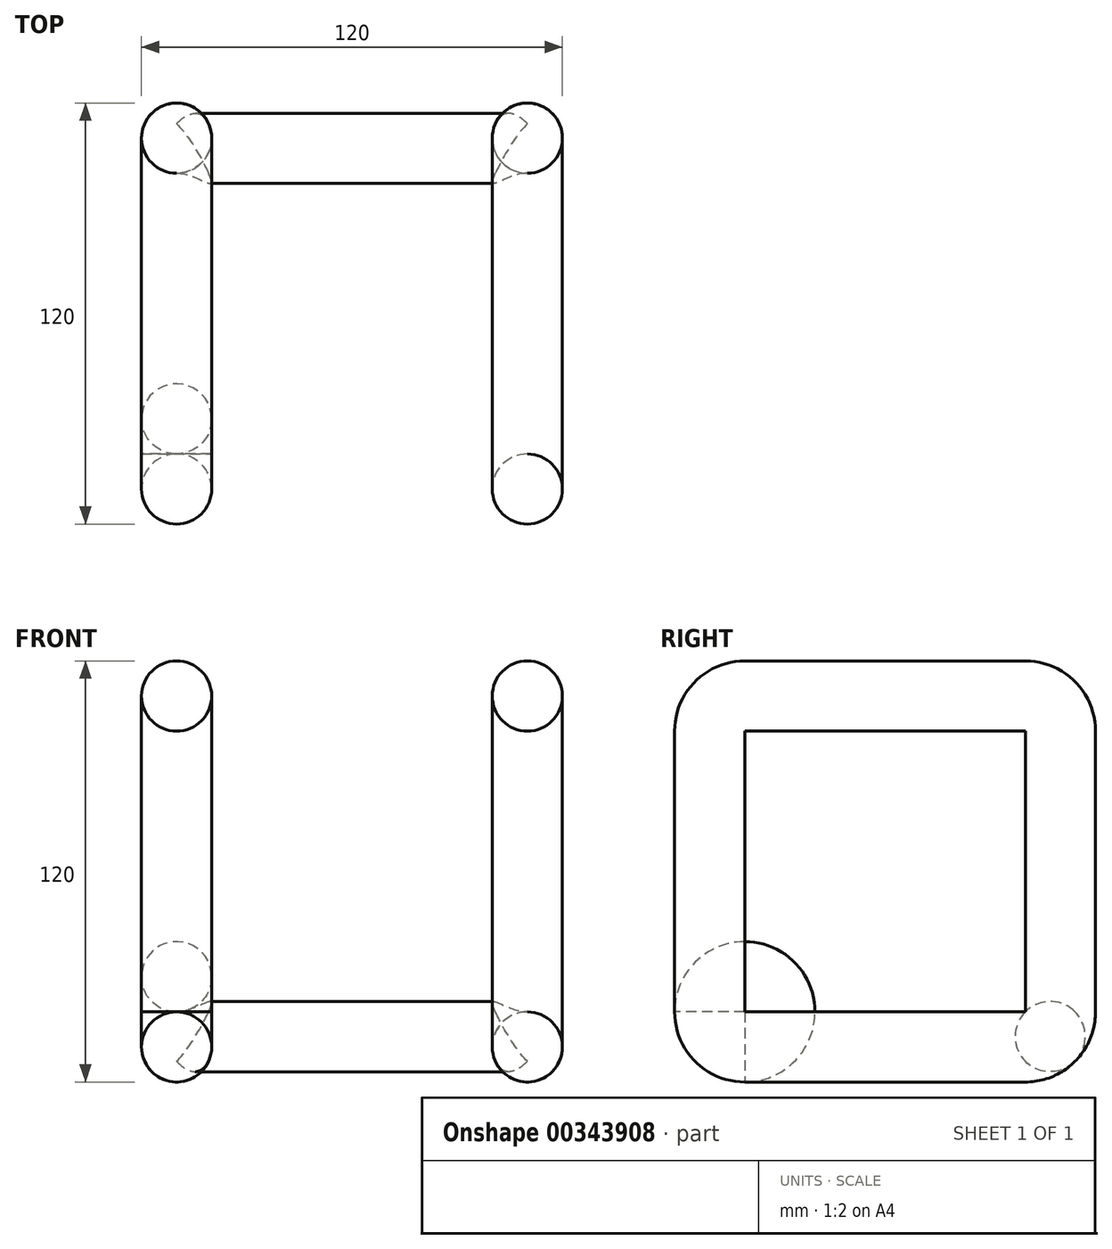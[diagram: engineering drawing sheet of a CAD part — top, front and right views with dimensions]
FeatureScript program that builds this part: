
annotation { "Feature Type Name" : "Feature", "Feature Type Description" : "" }
export const myFeature = defineFeature(function(context is Context, id is Id, definition is map)
    precondition{}
    {
        {
            var Q0;
            Q0=qCreatedBy(makeId("Front.planeOp"),FACE);
            var sketch = newSketch(context, id + "F0", { "sketchPlane" : qUnion([Q0])});
            skCircle(sketch, "E0", {"center": v(0, 0) * mm, "radius": 10 * mm});
            skSolve(sketch);
        }
        {
            var Q0;
            Q0 = qSketchRegion(id + "F0", true);
            extrude(context, id + "F1", {"entities" : qUnion([Q0]), "endBound" : BoundingType.SYMMETRIC, "depth" : 80 * mm});
        }
        {
            var Q0;
            Q0=makeQuery(id+"F1.opExtrude","CAP_FACE",FACE,{"disambiguationData":[OSD([sQuery(id+"F0.wireOp",EDGE,"E0")])],"isStart":true});
            var sketch = newSketch(context, id + "F2", { "sketchPlane" : qUnion([Q0])});
            skCircle(sketch, "E1", {"center": v(0, 0) * mm, "radius": 10 * mm});
            skSolve(sketch);
        }
        {
            var Q0;
            Q0=qCreatedBy(makeId("Right.planeOp"),FACE);
            var sketch = newSketch(context, id + "F3", { "sketchPlane" : qUnion([Q0])});
            skArc(sketch, "E2", {"start": v(40, 0) * mm, "mid": v(47.07, 2.93) * mm, "end": v(50, 10) * mm});
            skSolve(sketch);
        }
        {
            var Q0;
            Q0=makeQuery(id+"F2.imprint","IMPRINT",FACE,{"disambiguationData":[TD([[makeQuery(id+"F2.imprint","IMPRINT",EDGE,{"derivedFrom":sQuery(id+"F2.wireOp",EDGE,"E1")}),-1.0]])]});
            var Q1;
            Q1=sQuery(id+"F3.wireOp",EDGE,"E2");
            sweep(context, id + "F4", {"operationType" : NewBodyOperationType.ADD, "profiles" : qUnion([Q0]), "path" : qUnion([Q1])});
        }
        {
            var Q0;
            Q0=makeQuery(id+"F4.opSweep","CAP_FACE",FACE,{"disambiguationData":[OSD([sQuery(id+"F2.wireOp",EDGE,"E1"),sQuery(id+"F3.wireOp",VERTEX,"E2.end")])],"isStart":false});
            var sketch = newSketch(context, id + "F5", { "sketchPlane" : qUnion([Q0])});
            skCircle(sketch, "E3", {"center": v(0, 50) * mm, "radius": 10 * mm});
            skSolve(sketch);
        }
        {
            var Q0;
            Q0 = qSketchRegion(id + "F5", true);
            extrude(context, id + "F6", {"entities" : qUnion([Q0]), "operationType" : NewBodyOperationType.ADD, "depth" : 80 * mm});
        }
        {
            var Q0;
            Q0=makeQuery(id+"F6.opExtrude","CAP_FACE",FACE,{"disambiguationData":[OSD([sQuery(id+"F5.wireOp",EDGE,"E3")])],"isStart":false});
            var sketch = newSketch(context, id + "F7", { "sketchPlane" : qUnion([Q0])});
            skCircle(sketch, "E4", {"center": v(0, 50) * mm, "radius": 10 * mm});
            skSolve(sketch);
        }
        {
            var Q0;
            Q0=qCreatedBy(makeId("Right.planeOp"),FACE);
            var sketch = newSketch(context, id + "F8", { "sketchPlane" : qUnion([Q0])});
            skArc(sketch, "E5", {"start": v(50, 90) * mm, "mid": v(47.07, 97.07) * mm, "end": v(40, 100) * mm});
            skSolve(sketch);
        }
        {
            var Q0;
            Q0=qCreatedBy(makeId("Front.planeOp"),FACE);
            cPlane(context, id + "F9", {"entities" : qUnion([Q0]), "cplaneType" : CPlaneType.OFFSET, "offset" : 50 * mm, "oppositeDirection" : true, "width" : 150 * mm, "height" : 150 * mm});
        }
        {
            var Q0;
            Q0=makeQuery(id+"F7.imprint","IMPRINT",FACE,{"disambiguationData":[TD([[makeQuery(id+"F7.imprint","IMPRINT",EDGE,{"derivedFrom":sQuery(id+"F7.wireOp",EDGE,"E4")}),1.0]])]});
            var Q1;
            Q1=sQuery(id+"F8.wireOp",EDGE,"E5");
            sweep(context, id + "F10", {"operationType" : NewBodyOperationType.ADD, "profiles" : qUnion([Q0]), "path" : qUnion([Q1])});
        }
        {
            var Q0;
            Q0=makeQuery(id+"F1.opExtrude","SWEPT_BODY",BODY,{"disambiguationData":[OSD([sQuery(id+"F0.wireOp",EDGE,"E0")])]});
            var Q1;
            Q1=qCreatedBy(makeId("Front.planeOp"),FACE);
            mirror(context, id + "F11", {"operationType" : NewBodyOperationType.ADD, "entities" : qUnion([Q0]), "mirrorPlane" : qUnion([Q1])});
        }
        {
            var Q0;
            Q0=makeQuery(id+"F10.opSweep","CAP_FACE",FACE,{"disambiguationData":[OSD([sQuery(id+"F7.wireOp",EDGE,"E4"),sQuery(id+"F8.wireOp",VERTEX,"E5.end")])],"isStart":false});
            var sketch = newSketch(context, id + "F12", { "sketchPlane" : qUnion([Q0])});
            skCircle(sketch, "E6", {"center": v(0, 100) * mm, "radius": 10 * mm});
            skSolve(sketch);
        }
        {
            var Q0;
            Q0 = qSketchRegion(id + "F12", true);
            extrude(context, id + "F13", {"entities" : qUnion([Q0]), "operationType" : NewBodyOperationType.ADD, "depth" : 80 * mm});
        }
        {
            var Q0;
            Q0=qCreatedBy(makeId("Right.planeOp"),FACE);
            var sketch = newSketch(context, id + "F14", { "sketchPlane" : qUnion([Q0])});
            skArc(sketch, "E7", {"start": v(40, -10) * mm, "mid": v(54.14, -4.14) * mm, "end": v(60, 10) * mm});
            skCircle(sketch, "E8", {"center": v(47.07, 2.93) * mm, "radius": 10 * mm});
            skLineSegment(sketch, "E9", {"start": v(40, 10) * mm, "end": v(47.07, 2.93) * mm});
            skSolve(sketch);
        }
        {
            var Q0;
            Q0 = qSketchRegion(id + "F14", true);
            extrude(context, id + "F15", {"entities" : qUnion([Q0]), "operationType" : NewBodyOperationType.ADD, "depth" : 50 * mm});
        }
        {
            var Q0;
            Q0=makeQuery(id+"F1.opExtrude","SWEPT_BODY",BODY,{"disambiguationData":[OSD([sQuery(id+"F0.wireOp",EDGE,"E0")])]});
            var Q1;
            Q1=makeQuery(id+"F15.opExtrude","CAP_FACE",FACE,{"disambiguationData":[OSD([sQuery(id+"F14.wireOp",EDGE,"E8")])],"isStart":false});
            mirror(context, id + "F16", {"operationType" : NewBodyOperationType.ADD, "entities" : qUnion([Q0]), "mirrorPlane" : qUnion([Q1])});
        }
        {
            var Q0;
            Q0=qCreatedBy(makeId("Right.planeOp"),FACE);
            cPlane(context, id + "F17", {"entities" : qUnion([Q0]), "cplaneType" : CPlaneType.OFFSET, "offset" : 10 * mm, "oppositeDirection" : true, "width" : 150 * mm, "height" : 150 * mm});
        }
    });
